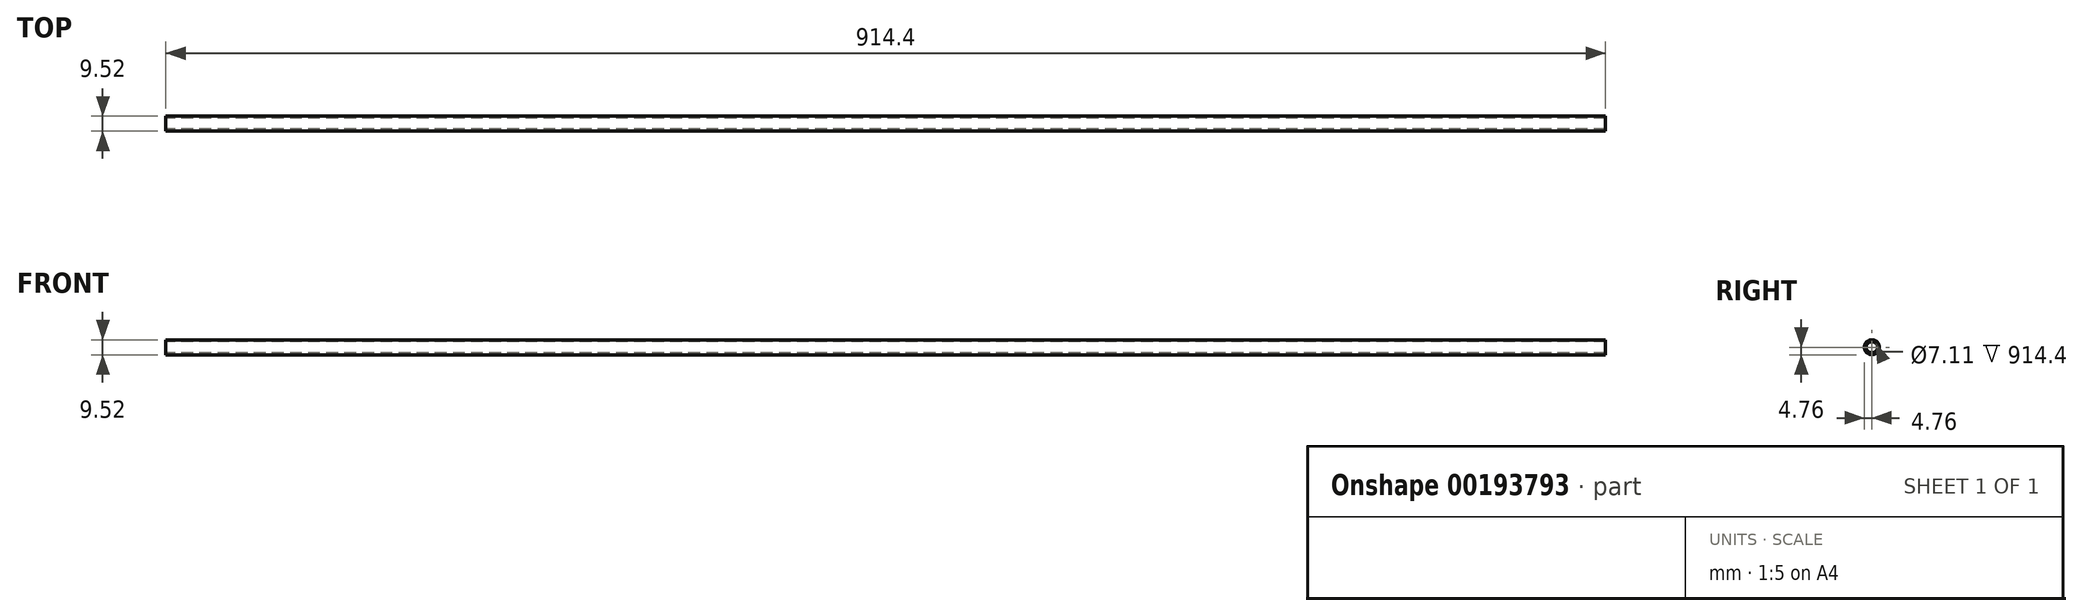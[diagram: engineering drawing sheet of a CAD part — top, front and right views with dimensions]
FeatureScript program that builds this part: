
annotation { "Feature Type Name" : "Feature", "Feature Type Description" : "" }
export const myFeature = defineFeature(function(context is Context, id is Id, definition is map)
    precondition{}
    {
        {
            var Q0;
            Q0=qCreatedBy(makeId("Right.planeOp"),FACE);
            var sketch = newSketch(context, id + "F0", { "sketchPlane" : qUnion([Q0])});
            skCircle(sketch, "E0", {"center": v(0, 0) * mm, "radius": 3.56 * mm});
            skCircle(sketch, "E1", {"center": v(0, 0) * mm, "radius": 4.76 * mm});
            skSolve(sketch);
        }
        {
            var Q0;
            Q0=makeQuery(id+"F0.imprint","IMPRINT",FACE,{"disambiguationData":[TD([[makeQuery(id+"F0.imprint","IMPRINT",EDGE,{"derivedFrom":sQuery(id+"F0.wireOp",EDGE,"E0")}),-1.0]])]});
            extrude(context, id + "F1", {"entities" : qUnion([Q0]), "depth" : 914.4 * mm});
        }
    });
